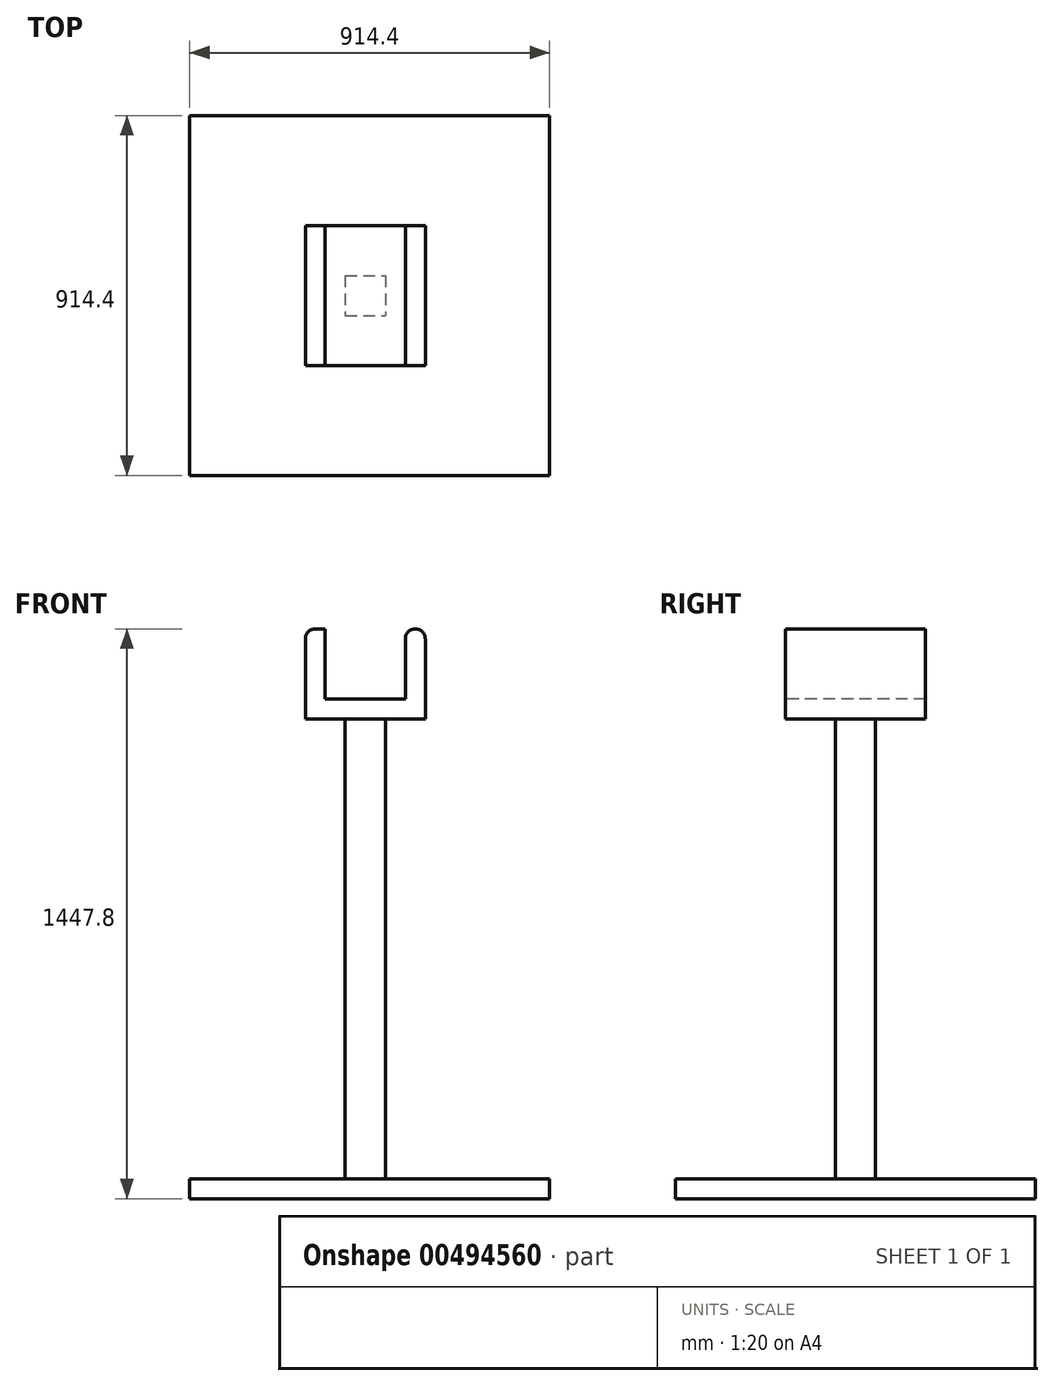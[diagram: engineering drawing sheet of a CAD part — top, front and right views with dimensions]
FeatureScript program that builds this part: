
annotation { "Feature Type Name" : "Feature", "Feature Type Description" : "" }
export const myFeature = defineFeature(function(context is Context, id is Id, definition is map)
    precondition{}
    {
        {
            var Q0;
            Q0=qCreatedBy(makeId("Top.planeOp"),FACE);
            var sketch = newSketch(context, id + "F0", { "sketchPlane" : qUnion([Q0])});
            skLineSegment(sketch, "E0.bottom", {"start": v(-445.84, 457.2) * mm, "end": v(468.56, 457.2) * mm});
            skLineSegment(sketch, "E0.top", {"start": v(-445.84, -457.2) * mm, "end": v(468.56, -457.2) * mm});
            skLineSegment(sketch, "E0.left", {"start": v(-445.84, 457.2) * mm, "end": v(-445.84, -457.2) * mm});
            skLineSegment(sketch, "E0.right", {"start": v(468.56, 457.2) * mm, "end": v(468.56, -457.2) * mm});
            skPoint(sketch, "E0.middle", {"position": v(11.36, 0) * mm});
            skSolve(sketch);
        }
        {
            var Q0;
            Q0 = qSketchRegion(id + "F0", true);
            var Q1;
            Q1 = qSketchRegion(id + "F2", true);
            extrude(context, id + "F1", {"entities" : qUnion([Q0, Q1]), "depth" : 50.8 * mm, "offsetDistance" : 25.4 * mm});
        }
        {
            var Q0;
            Q0=makeQuery(id+"F1.opExtrude","CAP_FACE",FACE,{"disambiguationData":[OSD([sQuery(id+"F0.wireOp",EDGE,"E0.bottom"),sQuery(id+"F0.wireOp",EDGE,"E0.top"),sQuery(id+"F0.wireOp",EDGE,"E0.left"),sQuery(id+"F0.wireOp",EDGE,"E0.right")])],"isStart":true});
            var sketch = newSketch(context, id + "F2", { "sketchPlane" : qUnion([Q0])});
            skLineSegment(sketch, "E1.bottom", {"start": v(50.8, 50.8) * mm, "end": v(-50.8, 50.8) * mm});
            skLineSegment(sketch, "E1.top", {"start": v(50.8, -50.8) * mm, "end": v(-50.8, -50.8) * mm});
            skLineSegment(sketch, "E1.left", {"start": v(50.8, 50.8) * mm, "end": v(50.8, -50.8) * mm});
            skLineSegment(sketch, "E1.right", {"start": v(-50.8, 50.8) * mm, "end": v(-50.8, -50.8) * mm});
            skPoint(sketch, "E1.middle", {"position": v(0, 0) * mm});
            skSolve(sketch);
        }
        {
            var Q0;
            Q0 = qSketchRegion(id + "F2", true);
            extrude(context, id + "F3", {"entities" : qUnion([Q0]), "operationType" : NewBodyOperationType.ADD, "depth" : -1219.2 * mm, "offsetDistance" : 25.4 * mm});
        }
        {
            var Q0;
            Q0=makeQuery(id+"F3.opExtrude","CAP_FACE",FACE,{"disambiguationData":[OSD([sQuery(id+"F2.wireOp",EDGE,"E1.bottom"),sQuery(id+"F2.wireOp",EDGE,"E1.top"),sQuery(id+"F2.wireOp",EDGE,"E1.left"),sQuery(id+"F2.wireOp",EDGE,"E1.right")])],"isStart":false});
            var sketch = newSketch(context, id + "F4", { "sketchPlane" : qUnion([Q0])});
            skLineSegment(sketch, "E2.bottom", {"start": v(-152.4, 177.8) * mm, "end": v(152.4, 177.8) * mm});
            skLineSegment(sketch, "E2.top", {"start": v(-152.4, -177.8) * mm, "end": v(152.4, -177.8) * mm});
            skLineSegment(sketch, "E2.left", {"start": v(-152.4, 177.8) * mm, "end": v(-152.4, -177.8) * mm});
            skLineSegment(sketch, "E2.right", {"start": v(152.4, 177.8) * mm, "end": v(152.4, -177.8) * mm});
            skPoint(sketch, "E2.middle", {"position": v(0, 0) * mm});
            skSolve(sketch);
        }
        {
            var Q0;
            Q0 = qSketchRegion(id + "F4", true);
            extrude(context, id + "F5", {"entities" : qUnion([Q0]), "operationType" : NewBodyOperationType.ADD, "depth" : 228.6 * mm, "offsetDistance" : 25.4 * mm});
        }
        {
            var Q0;
            Q0=makeQuery(id+"F5.opExtrude","CAP_FACE",FACE,{"disambiguationData":[OSD([sQuery(id+"F4.wireOp",EDGE,"E2.bottom"),sQuery(id+"F4.wireOp",EDGE,"E2.top"),sQuery(id+"F4.wireOp",EDGE,"E2.left"),sQuery(id+"F4.wireOp",EDGE,"E2.right")])],"isStart":false});
            var sketch = newSketch(context, id + "F6", { "sketchPlane" : qUnion([Q0])});
            skLineSegment(sketch, "E3.bottom", {"start": v(101.6, 177.8) * mm, "end": v(-101.6, 177.8) * mm});
            skLineSegment(sketch, "E3.top", {"start": v(101.6, -177.8) * mm, "end": v(-101.6, -177.8) * mm});
            skLineSegment(sketch, "E3.left", {"start": v(101.6, 177.8) * mm, "end": v(101.6, -177.8) * mm});
            skLineSegment(sketch, "E3.right", {"start": v(-101.6, 177.8) * mm, "end": v(-101.6, -177.8) * mm});
            skPoint(sketch, "E3.middle", {"position": v(0, 0) * mm});
            skSolve(sketch);
        }
        {
            var Q0;
            Q0 = qSketchRegion(id + "F6", true);
            extrude(context, id + "F7", {"entities" : qUnion([Q0]), "operationType" : NewBodyOperationType.REMOVE, "oppositeDirection" : true, "depth" : 177.8 * mm, "offsetDistance" : 25.4 * mm});
        }
        {
            var Q0;
            Q0=makeQuery(id+"F5.opExtrude","CAP_EDGE",EDGE,{"disambiguationData":[OSD([sQuery(id+"F4.wireOp",EDGE,"E2.left")])],"isStart":false});
            var Q1;
            Q1=makeQuery(id+"F7.boolean.opBoolean","COPY",EDGE,{"derivedFrom":makeQuery(id+"F7.opExtrude","CAP_EDGE",EDGE,{"disambiguationData":[OSD([sQuery(id+"F6.wireOp",EDGE,"E3.right")])],"isStart":true})});
            var Q2;
            Q2=makeQuery(id+"F7.boolean.opBoolean","COPY",EDGE,{"derivedFrom":makeQuery(id+"F7.opExtrude","CAP_EDGE",EDGE,{"disambiguationData":[OSD([sQuery(id+"F6.wireOp",EDGE,"E3.left")])],"isStart":true})});
            var Q3;
            Q3=makeQuery(id+"F5.opExtrude","CAP_EDGE",EDGE,{"disambiguationData":[OSD([sQuery(id+"F4.wireOp",EDGE,"E2.right")])],"isStart":false});
            fillet(context, id + "F8", {"entities" : qUnion([Q0, Q1, Q2, Q3]), "radius" : 25.4 * mm, "tangentPropagation" : true, "allowEdgeOverflow" : false});
        }
    });
